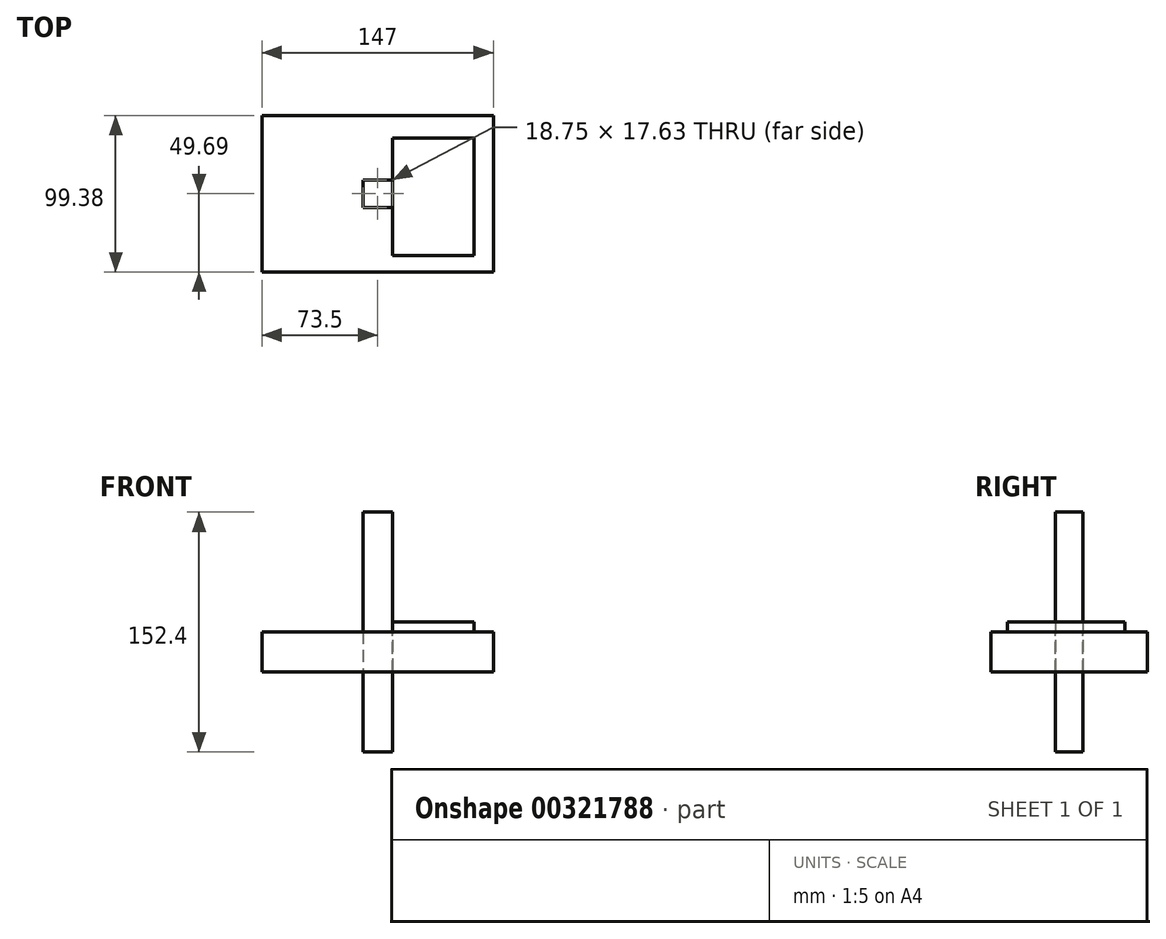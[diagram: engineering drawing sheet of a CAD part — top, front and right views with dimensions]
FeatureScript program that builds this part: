
annotation { "Feature Type Name" : "Feature", "Feature Type Description" : "" }
export const myFeature = defineFeature(function(context is Context, id is Id, definition is map)
    precondition{}
    {
        {
            var Q0;
            Q0=qCreatedBy(makeId("Top.planeOp"),FACE);
            var sketch = newSketch(context, id + "F0", { "sketchPlane" : qUnion([Q0])});
            skLineSegment(sketch, "E0.bottom", {"start": v(73.5, -49.69) * mm, "end": v(-73.5, -49.69) * mm});
            skLineSegment(sketch, "E0.top", {"start": v(73.5, 49.69) * mm, "end": v(-73.5, 49.69) * mm});
            skLineSegment(sketch, "E0.left", {"start": v(73.5, -49.69) * mm, "end": v(73.5, 49.69) * mm});
            skLineSegment(sketch, "E0.right", {"start": v(-73.5, -49.69) * mm, "end": v(-73.5, 49.69) * mm});
            skPoint(sketch, "E0.middle", {"position": v(0, 0) * mm});
            skLineSegment(sketch, "E1.bottom", {"start": v(9.38, -8.81) * mm, "end": v(-9.38, -8.81) * mm});
            skLineSegment(sketch, "E1.top", {"start": v(9.38, 8.81) * mm, "end": v(-9.38, 8.81) * mm});
            skLineSegment(sketch, "E1.left", {"start": v(9.38, -8.81) * mm, "end": v(9.38, 8.81) * mm});
            skLineSegment(sketch, "E1.right", {"start": v(-9.38, -8.81) * mm, "end": v(-9.38, 8.81) * mm});
            skLineSegment(sketch, "E2.bottom", {"start": v(9.38, -39.19) * mm, "end": v(61.13, -39.19) * mm});
            skLineSegment(sketch, "E2.top", {"start": v(9.38, 35.44) * mm, "end": v(61.13, 35.44) * mm});
            skLineSegment(sketch, "E2.left", {"start": v(9.38, -39.19) * mm, "end": v(9.38, 35.44) * mm});
            skLineSegment(sketch, "E2.right", {"start": v(61.13, -39.19) * mm, "end": v(61.13, 35.44) * mm});
            skSolve(sketch);
        }
        {
            var Q0;
            Q0=makeQuery(id+"F0.imprint","IMPRINT",FACE,{"disambiguationData":[TD([[makeQuery(id+"F0.imprint","IMPRINT",EDGE,{"derivedFrom":sQuery(id+"F0.wireOp",EDGE,"E0.bottom")}),-1.0]])]});
            var Q1;
            {var subQ3=sQuery(id+"F0.wireOp",EDGE,"E2.bottom");Q1=makeQuery(id+"F0.imprint","IMPRINT",FACE,{"disambiguationData":[TD([[makeQuery(id+"F0.imprint","IMPRINT",EDGE,{"derivedFrom":subQ3}),1.0]])]});}
            extrude(context, id + "F1", {"entities" : qUnion([Q0, Q1]), "oppositeDirection" : true, "depth" : 25.4 * mm});
        }
        {
            var Q0;
            {var subQ0=sQuery(id+"F0.wireOp",EDGE,"E1.bottom");Q0=makeQuery(id+"F0.imprint","IMPRINT",FACE,{"disambiguationData":[TD([[makeQuery(id+"F0.imprint","IMPRINT",EDGE,{"derivedFrom":subQ0}),-1.0]])]});}
            extrude(context, id + "F2", {"entities" : qUnion([Q0]), "endBound" : BoundingType.SYMMETRIC, "depth" : 152.4 * mm});
        }
        {
            var Q0;
            {var subQ3=sQuery(id+"F0.wireOp",EDGE,"E2.bottom");Q0=makeQuery(id+"F0.imprint","IMPRINT",FACE,{"disambiguationData":[TD([[makeQuery(id+"F0.imprint","IMPRINT",EDGE,{"derivedFrom":subQ3}),1.0]])]});}
            extrude(context, id + "F3", {"entities" : qUnion([Q0]), "depth" : 6.35 * mm});
        }
    });
